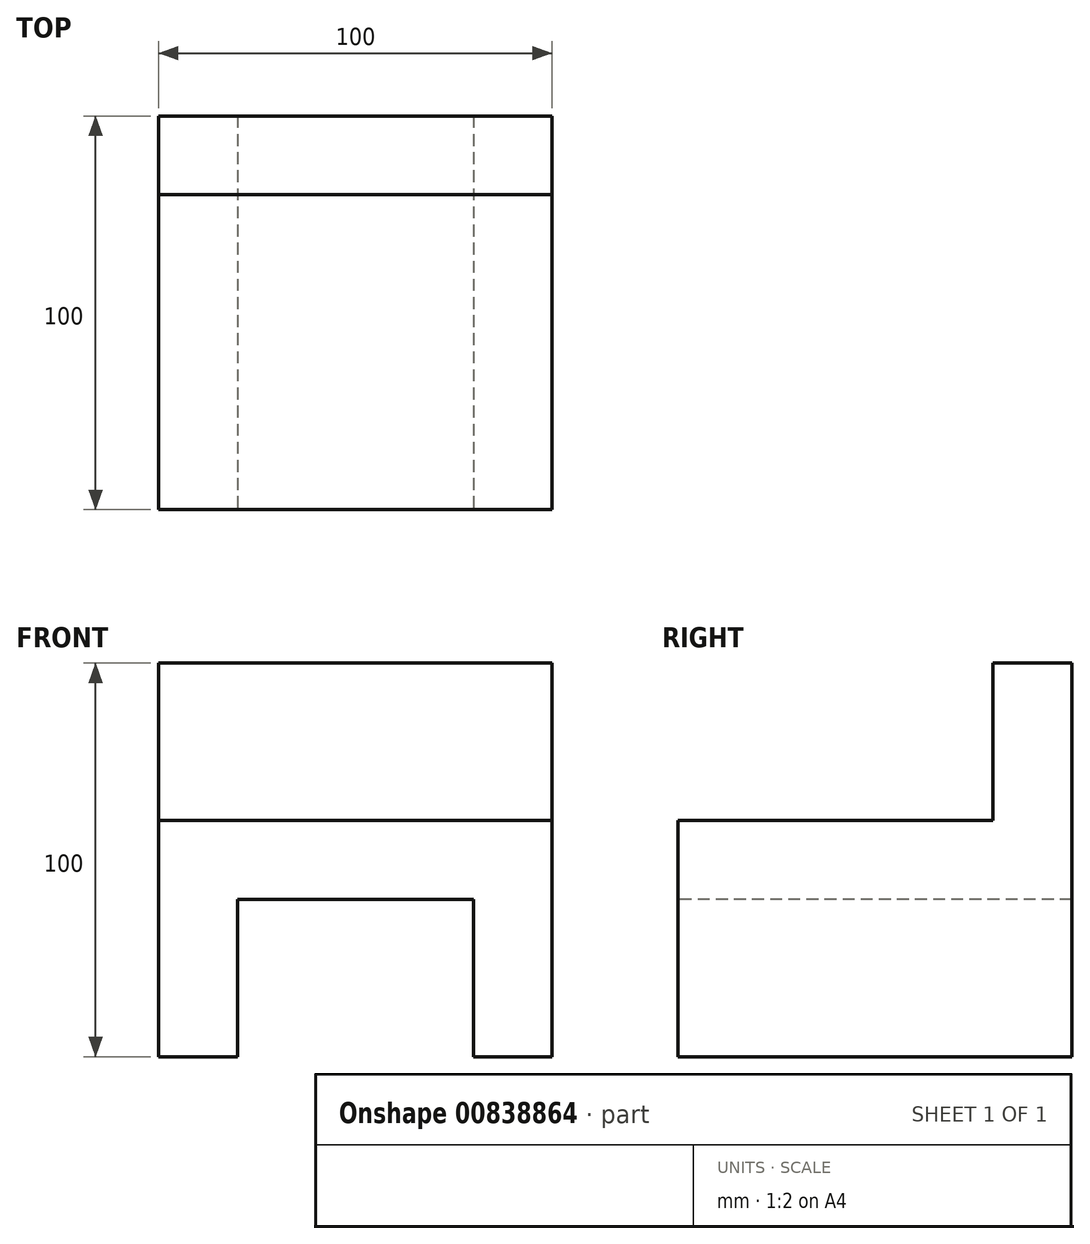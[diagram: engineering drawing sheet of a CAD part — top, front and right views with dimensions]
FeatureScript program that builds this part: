
annotation { "Feature Type Name" : "Feature", "Feature Type Description" : "" }
export const myFeature = defineFeature(function(context is Context, id is Id, definition is map)
    precondition{}
    {
        {
            var Q0;
            Q0=qCreatedBy(makeId("Top.planeOp"),FACE);
            var sketch = newSketch(context, id + "F0", { "sketchPlane" : qUnion([Q0])});
            skLineSegment(sketch, "E0.bottom", {"start": v(50, -50) * mm, "end": v(-50, -50) * mm});
            skLineSegment(sketch, "E0.top", {"start": v(50, 50) * mm, "end": v(-50, 50) * mm});
            skLineSegment(sketch, "E0.left", {"start": v(50, -50) * mm, "end": v(50, 50) * mm});
            skLineSegment(sketch, "E0.right", {"start": v(-50, -50) * mm, "end": v(-50, 50) * mm});
            skPoint(sketch, "E0.middle", {"position": v(0, 0) * mm});
            skSolve(sketch);
        }
        {
            var Q0;
            Q0 = qSketchRegion(id + "F0", true);
            extrude(context, id + "F1", {"entities" : qUnion([Q0]), "depth" : 100 * mm, "offsetDistance" : 25 * mm});
        }
        {
            var Q0;
            Q0=makeQuery(id+"F1.opExtrude","CAP_FACE",FACE,{"disambiguationData":[OSD([sQuery(id+"F0.wireOp",EDGE,"E0.bottom"),sQuery(id+"F0.wireOp",EDGE,"E0.top"),sQuery(id+"F0.wireOp",EDGE,"E0.left"),sQuery(id+"F0.wireOp",EDGE,"E0.right")])],"isStart":false});
            var sketch = newSketch(context, id + "F2", { "sketchPlane" : qUnion([Q0])});
            skLineSegment(sketch, "E1.bottom", {"start": v(-50, -50) * mm, "end": v(50, -50) * mm});
            skLineSegment(sketch, "E1.top", {"start": v(-50, 30) * mm, "end": v(50, 30) * mm});
            skLineSegment(sketch, "E1.left", {"start": v(-50, -50) * mm, "end": v(-50, 30) * mm});
            skLineSegment(sketch, "E1.right", {"start": v(50, -50) * mm, "end": v(50, 30) * mm});
            skSolve(sketch);
        }
        {
            var Q0;
            Q0 = qSketchRegion(id + "F2", true);
            extrude(context, id + "F3", {"entities" : qUnion([Q0]), "operationType" : NewBodyOperationType.REMOVE, "oppositeDirection" : true, "depth" : 40 * mm, "offsetDistance" : 25 * mm});
        }
        {
            var Q0;
            Q0=makeQuery(id+"F1.opExtrude","SWEPT_FACE",FACE,{"disambiguationData":[OSD([sQuery(id+"F0.wireOp",EDGE,"E0.bottom")])]});
            var sketch = newSketch(context, id + "F4", { "sketchPlane" : qUnion([Q0])});
            skLineSegment(sketch, "E2.bottom", {"start": v(-30, 40) * mm, "end": v(30, 40) * mm});
            skLineSegment(sketch, "E2.top", {"start": v(-30, 0) * mm, "end": v(30, 0) * mm});
            skLineSegment(sketch, "E2.left", {"start": v(-30, 40) * mm, "end": v(-30, 0) * mm});
            skLineSegment(sketch, "E2.right", {"start": v(30, 40) * mm, "end": v(30, 0) * mm});
            skSolve(sketch);
        }
        {
            var Q0;
            Q0=makeQuery(id+"F4.imprint","IMPRINT",FACE,{"disambiguationData":[TD([[makeQuery(id+"F4.imprint","IMPRINT",EDGE,{"derivedFrom":sQuery(id+"F4.wireOp",EDGE,"E2.bottom")}),-1.0]])]});
            extrude(context, id + "F5", {"entities" : qUnion([Q0]), "operationType" : NewBodyOperationType.REMOVE, "oppositeDirection" : true, "depth" : 2000 * mm, "offsetDistance" : 25 * mm});
        }
    });
